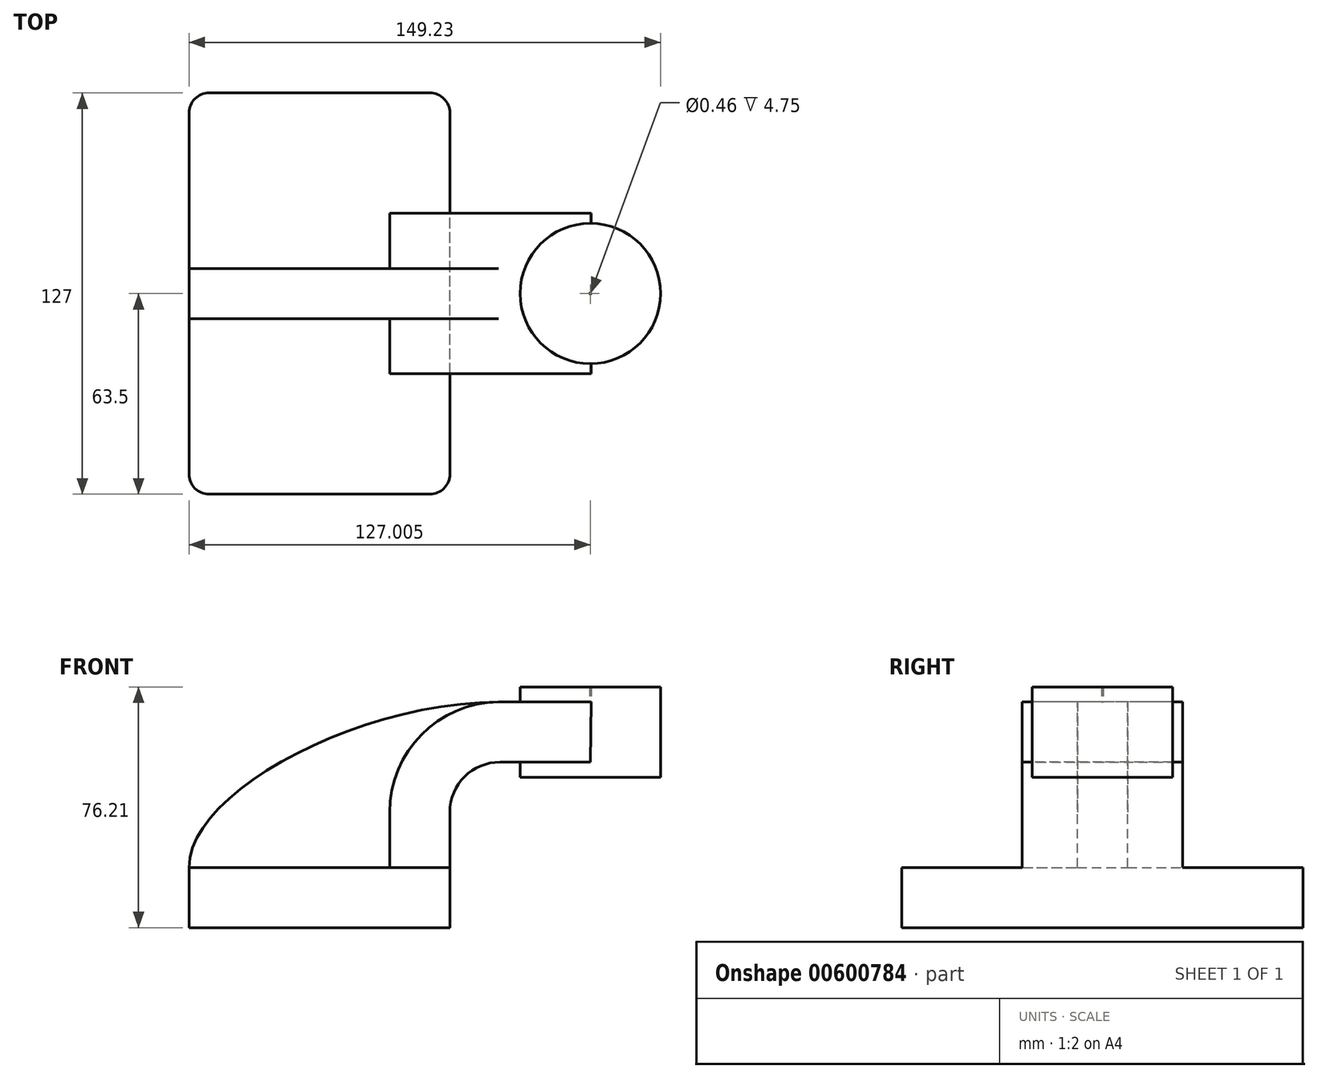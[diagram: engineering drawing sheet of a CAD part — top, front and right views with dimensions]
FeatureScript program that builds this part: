
annotation { "Feature Type Name" : "Feature", "Feature Type Description" : "" }
export const myFeature = defineFeature(function(context is Context, id is Id, definition is map)
    precondition{}
    {
        {
            var Q0;
            Q0=qCreatedBy(makeId("Front.planeOp"),FACE);
            var sketch = newSketch(context, id + "F0", { "sketchPlane" : qUnion([Q0])});
            skLineSegment(sketch, "E0.bottom", {"start": v(-41.28, -9.53) * mm, "end": v(41.28, -9.53) * mm});
            skLineSegment(sketch, "E0.top", {"start": v(-41.28, 9.52) * mm, "end": v(41.28, 9.52) * mm});
            skLineSegment(sketch, "E0.left", {"start": v(-41.28, -9.53) * mm, "end": v(-41.28, 9.52) * mm});
            skLineSegment(sketch, "E0.right", {"start": v(41.28, -9.53) * mm, "end": v(41.28, 9.52) * mm});
            skPoint(sketch, "E0.middle", {"position": v(0, 0) * mm});
            skLineSegment(sketch, "E1.bottom", {"start": v(107.95, 38.1) * mm, "end": v(57.15, 38.1) * mm});
            skLineSegment(sketch, "E1.top", {"start": v(107.95, 66.67) * mm, "end": v(57.15, 66.67) * mm});
            skLineSegment(sketch, "E1.left", {"start": v(107.95, 38.1) * mm, "end": v(107.95, 66.68) * mm});
            skLineSegment(sketch, "E1.right", {"start": v(57.15, 38.1) * mm, "end": v(57.15, 66.67) * mm});
            skPoint(sketch, "E1.middle", {"position": v(82.55, 52.39) * mm});
            skLineSegment(sketch, "E2", {"start": v(41.28, 9.52) * mm, "end": v(41.28, 27) * mm});
            skArc(sketch, "E3", {"start": v(41.28, 27) * mm, "mid": v(45.92, 38.23) * mm, "end": v(57.15, 42.88) * mm});
            skLineSegment(sketch, "E4.0", {"start": v(57.15, 61.93) * mm, "end": v(85.96, 61.93) * mm});
            skArc(sketch, "E4.1", {"start": v(22.23, 27) * mm, "mid": v(32.45, 51.7) * mm, "end": v(57.15, 61.93) * mm});
            skLineSegment(sketch, "E4.2", {"start": v(22.22, 9.52) * mm, "end": v(22.22, 27) * mm});
            skFitSpline(sketch, "E5", {"points": [v(-41.28, 9.53) * mm, v(57.15, 61.93) * mm], "startDerivative": vector(-1.06, 69.82) * mm, "endDerivative": vector(138.25, 0.6) * mm});
            skLineSegment(sketch, "E6", {"start": v(57.15, 42.88) * mm, "end": v(85.73, 42.88) * mm});
            skLineSegment(sketch, "E7", {"start": v(85.73, 38.1) * mm, "end": v(85.73, 42.88) * mm});
            skLineSegment(sketch, "E8", {"start": v(85.73, 42.88) * mm, "end": v(85.96, 61.93) * mm});
            skLineSegment(sketch, "E9", {"start": v(85.96, 61.93) * mm, "end": v(85.96, 66.67) * mm});
            skSolve(sketch);
        }
        {
            var Q0;
            Q0=makeQuery(id+"F0.imprint","IMPRINT",FACE,{"disambiguationData":[TD([[makeQuery(id+"F0.imprint","IMPRINT",EDGE,{"derivedFrom":sQuery(id+"F0.wireOp",EDGE,"E0.bottom")}),1.0]])]});
            extrude(context, id + "F1", {"entities" : qUnion([Q0]), "endBound" : BoundingType.SYMMETRIC, "depth" : 127 * mm, "offsetDistance" : 25.4 * mm});
        }
        {
            var Q0;
            {var subQ1=sQuery(id+"F0.wireOp",EDGE,"E2");Q0=makeQuery(id+"F0.imprint","IMPRINT",FACE,{"disambiguationData":[TD([[makeQuery(id+"F0.imprint","IMPRINT",EDGE,{"derivedFrom":subQ1}),1.0]])]});}
            var Q1;
            {var subQ2=sQuery(id+"F0.wireOp",EDGE,"E4.0");Q1=makeQuery(id+"F0.imprint","IMPRINT",FACE,{"disambiguationData":[TD([[makeQuery(id+"F0.imprint","IMPRINT",EDGE,{"derivedFrom":subQ2}),-1.0]])]});}
            extrude(context, id + "F2", {"entities" : qUnion([Q0, Q1]), "operationType" : NewBodyOperationType.ADD, "endBound" : BoundingType.SYMMETRIC, "depth" : 50.8 * mm, "offsetDistance" : 25.4 * mm});
        }
        {
            var Q0;
            {var subQ3=sQuery(id+"F0.wireOp",EDGE,"E4.2");Q0=makeQuery(id+"F0.imprint","IMPRINT",FACE,{"disambiguationData":[TD([[makeQuery(id+"F0.imprint","IMPRINT",EDGE,{"derivedFrom":subQ3}),1.0]])]});}
            extrude(context, id + "F3", {"entities" : qUnion([Q0]), "operationType" : NewBodyOperationType.ADD, "endBound" : BoundingType.SYMMETRIC, "depth" : 15.88 * mm, "offsetDistance" : 25.4 * mm});
        }
        {
            var Q0;
            {var subQ0=sQuery(id+"F0.wireOp",EDGE,"E1.left");Q0=makeQuery(id+"F0.imprint","IMPRINT",FACE,{"disambiguationData":[TD([[makeQuery(id+"F0.imprint","IMPRINT",EDGE,{"derivedFrom":subQ0}),1.0]])]});}
            var Q1;
            Q1=sQuery(id+"F0.wireOp",EDGE,"E7");
            revolve(context, id + "F4", {"operationType" : NewBodyOperationType.ADD, "entities" : qUnion([Q0]), "axis" : qUnion([Q1]), "revolveType" : RevolveType.FULL});
        }
        {
            var Q0;
            Q0=makeQuery(id+"F1.opExtrude","CAP_EDGE",EDGE,{"disambiguationData":[OSD([sQuery(id+"F0.wireOp",EDGE,"E0.left")])],"isStart":false});
            var Q1;
            Q1=makeQuery(id+"F1.opExtrude","CAP_EDGE",EDGE,{"disambiguationData":[OSD([sQuery(id+"F0.wireOp",EDGE,"E0.right")])],"isStart":false});
            var Q2;
            Q2=makeQuery(id+"F1.opExtrude","CAP_EDGE",EDGE,{"disambiguationData":[OSD([sQuery(id+"F0.wireOp",EDGE,"E0.right")])],"isStart":true});
            var Q3;
            Q3=makeQuery(id+"F1.opExtrude","CAP_EDGE",EDGE,{"disambiguationData":[OSD([sQuery(id+"F0.wireOp",EDGE,"E0.left")])],"isStart":true});
            fillet(context, id + "F5", {"entities" : qUnion([Q0, Q1, Q2, Q3]), "radius" : 6.35 * mm, "tangentPropagation" : true, "allowEdgeOverflow" : false});
        }
    });
